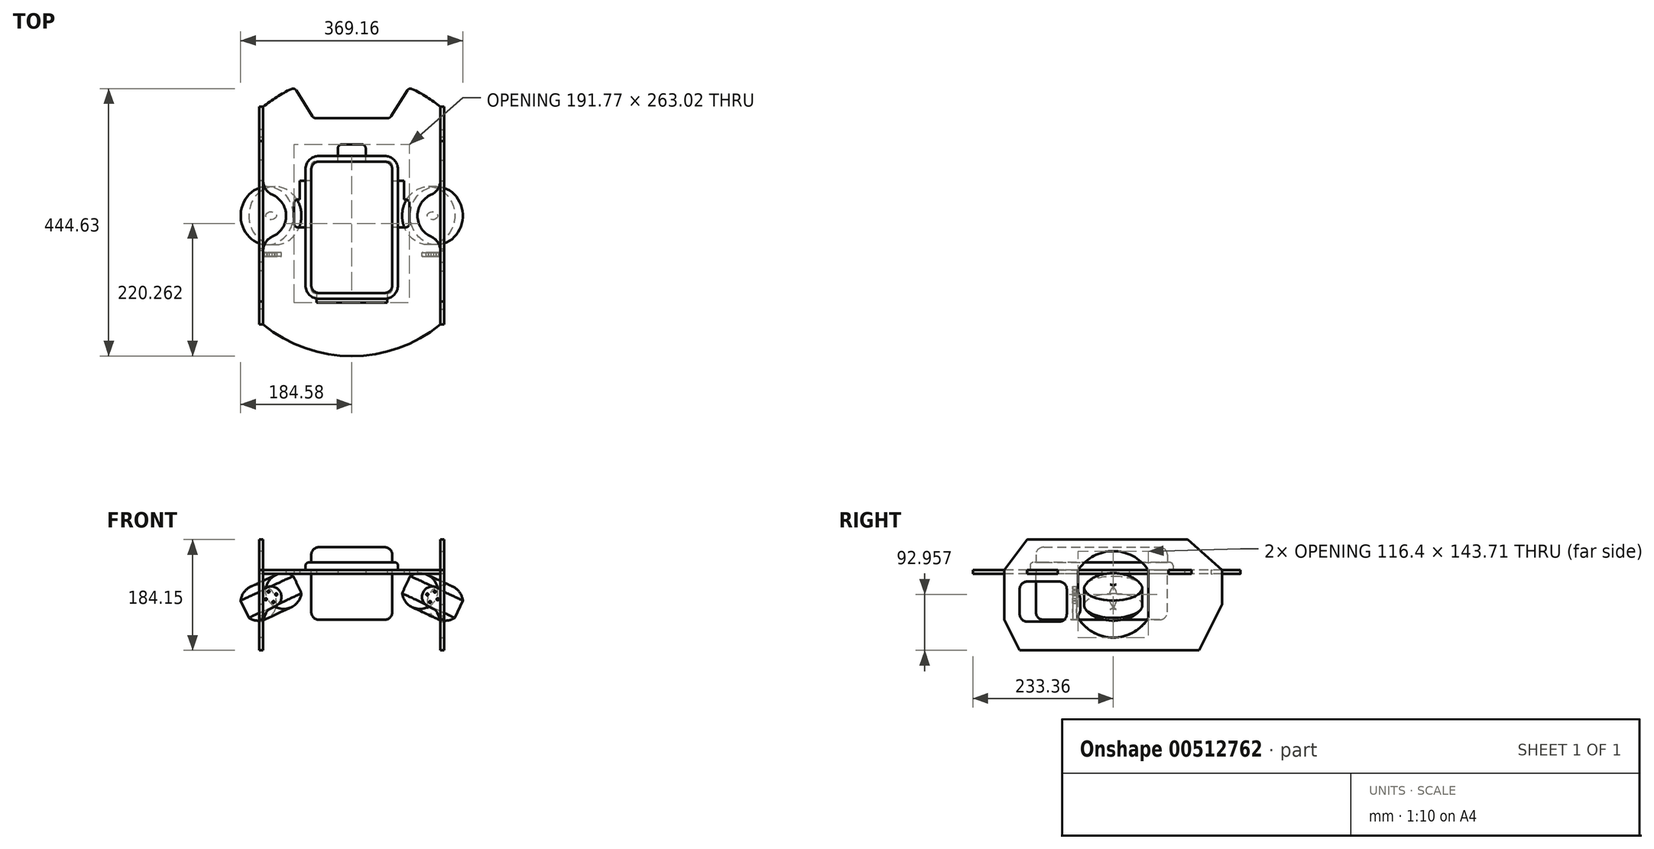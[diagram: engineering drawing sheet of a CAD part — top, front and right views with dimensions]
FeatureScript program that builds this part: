
annotation { "Feature Type Name" : "Feature", "Feature Type Description" : "" }
export const myFeature = defineFeature(function(context is Context, id is Id, definition is map)
    precondition{}
    {
        {
            var Q0;
            Q0=qCreatedBy(makeId("Top.planeOp"),FACE);
            var sketch = newSketch(context, id + "F0", { "sketchPlane" : qUnion([Q0])});
            skCircle(sketch, "E0", {"center": v(0, 0) * mm, "radius": 240 * mm, "construction": true});
            skSolve(sketch);
        }
        {
            var Q0;
            Q0=qCreatedBy(makeId("Top.planeOp"),FACE);
            var sketch = newSketch(context, id + "F1", { "sketchPlane" : qUnion([Q0])});
            skLineSegment(sketch, "E1", {"start": v(0, 0) * mm, "end": v(0, 264.4) * mm, "construction": true});
            skLineSegment(sketch, "E2", {"start": v(-67.31, 83.49) * mm, "end": v(-67.31, 58.09) * mm});
            skLineSegment(sketch, "E3", {"start": v(-67.3, 58.09) * mm, "end": v(-86.61, 58.09) * mm});
            skLineSegment(sketch, "E4", {"start": v(-86.61, 58.09) * mm, "end": v(-86.61, 26.84) * mm});
            skLineSegment(sketch, "E5", {"start": v(-86.61, 26.84) * mm, "end": v(-89.54, 26.84) * mm});
            skLineSegment(sketch, "E6", {"start": v(-95.89, 20.5) * mm, "end": v(-95.89, -13.03) * mm});
            skLineSegment(sketch, "E7", {"start": v(-89.54, -19.38) * mm, "end": v(-67.3, -19.38) * mm});
            skLineSegment(sketch, "E8", {"start": v(-67.31, -19.38) * mm, "end": v(-67.3, -122.25) * mm});
            skLineSegment(sketch, "E9", {"start": v(-60.96, -128.6) * mm, "end": v(-58.67, -128.6) * mm});
            skLineSegment(sketch, "E10", {"start": v(-60.96, 89.84) * mm, "end": v(-23.11, 89.84) * mm});
            skLineSegment(sketch, "E11", {"start": v(-23.11, 89.84) * mm, "end": v(-23.11, 112.06) * mm});
            skLineSegment(sketch, "E12.MirrorCS", {"start": v(86.61, 26.84) * mm, "end": v(89.54, 26.84) * mm});
            skLineSegment(sketch, "E13.MirrorCS", {"start": v(60.96, -128.6) * mm, "end": v(58.67, -128.6) * mm});
            skLineSegment(sketch, "E14.MirrorCS", {"start": v(67.31, 83.49) * mm, "end": v(67.31, 58.09) * mm});
            skLineSegment(sketch, "E15.MirrorCS", {"start": v(23.11, 89.84) * mm, "end": v(23.11, 112.06) * mm});
            skLineSegment(sketch, "E16.MirrorCS", {"start": v(67.3, 58.09) * mm, "end": v(86.61, 58.09) * mm});
            skLineSegment(sketch, "E17.MirrorCS", {"start": v(67.31, -19.38) * mm, "end": v(67.31, -122.25) * mm});
            skLineSegment(sketch, "E18.MirrorCS", {"start": v(89.54, -19.38) * mm, "end": v(67.3, -19.38) * mm});
            skLineSegment(sketch, "E19.MirrorCS", {"start": v(86.61, 58.09) * mm, "end": v(86.61, 26.84) * mm});
            skLineSegment(sketch, "E20.MirrorCS", {"start": v(95.89, 20.5) * mm, "end": v(95.89, -13.03) * mm});
            skLineSegment(sketch, "E21.MirrorCS", {"start": v(60.96, 89.84) * mm, "end": v(23.11, 89.84) * mm});
            skLineSegment(sketch, "E22", {"start": v(-58.67, -128.6) * mm, "end": v(-58.67, -144.6) * mm});
            skLineSegment(sketch, "E23.MirrorCS", {"start": v(58.67, -128.6) * mm, "end": v(58.67, -144.6) * mm});
            skLineSegment(sketch, "E24", {"start": v(-58.67, -144.6) * mm, "end": v(58.67, -144.6) * mm});
            skLineSegment(sketch, "E25", {"start": v(-16.76, 118.41) * mm, "end": v(16.76, 118.41) * mm});
            skPoint(sketch, "E26.visualSharp", {"position": v(-67.31, 89.84) * mm});
            skArc(sketch, "E26.filletArc", {"start": v(-60.96, 89.84) * mm, "mid": v(-65.45, 87.98) * mm, "end": v(-67.31, 83.49) * mm});
            skPoint(sketch, "E27.visualSharp", {"position": v(67.31, 89.84) * mm});
            skArc(sketch, "E27.filletArc", {"start": v(67.31, 83.49) * mm, "mid": v(65.45, 87.98) * mm, "end": v(60.96, 89.84) * mm});
            skPoint(sketch, "E28.visualSharp", {"position": v(23.11, 118.41) * mm});
            skArc(sketch, "E28.filletArc", {"start": v(23.11, 112.06) * mm, "mid": v(21.25, 116.55) * mm, "end": v(16.76, 118.41) * mm});
            skPoint(sketch, "E29.visualSharp", {"position": v(-23.11, 118.41) * mm});
            skArc(sketch, "E29.filletArc", {"start": v(-16.76, 118.41) * mm, "mid": v(-21.25, 116.55) * mm, "end": v(-23.11, 112.06) * mm});
            skPoint(sketch, "E30.visualSharp", {"position": v(-67.3, -128.6) * mm});
            skArc(sketch, "E30.filletArc", {"start": v(-67.3, -122.25) * mm, "mid": v(-65.45, -126.74) * mm, "end": v(-60.96, -128.6) * mm});
            skPoint(sketch, "E31.visualSharp", {"position": v(67.3, -128.6) * mm});
            skArc(sketch, "E31.filletArc", {"start": v(60.96, -128.6) * mm, "mid": v(65.45, -126.74) * mm, "end": v(67.31, -122.25) * mm});
            skPoint(sketch, "E32.visualSharp", {"position": v(95.89, -19.38) * mm});
            skArc(sketch, "E32.filletArc", {"start": v(89.54, -19.38) * mm, "mid": v(94.03, -17.52) * mm, "end": v(95.89, -13.03) * mm});
            skPoint(sketch, "E33.visualSharp", {"position": v(95.89, 26.84) * mm});
            skArc(sketch, "E33.filletArc", {"start": v(95.89, 20.5) * mm, "mid": v(94.03, 24.98) * mm, "end": v(89.54, 26.84) * mm});
            skPoint(sketch, "E34.visualSharp", {"position": v(-95.89, 26.84) * mm});
            skArc(sketch, "E34.filletArc", {"start": v(-89.54, 26.84) * mm, "mid": v(-94.03, 24.98) * mm, "end": v(-95.89, 20.5) * mm});
            skPoint(sketch, "E35.visualSharp", {"position": v(-95.89, -19.38) * mm});
            skArc(sketch, "E35.filletArc", {"start": v(-95.89, -13.03) * mm, "mid": v(-94.03, -17.52) * mm, "end": v(-89.54, -19.38) * mm});
            skLineSegment(sketch, "E36", {"start": v(-147.32, 180.98) * mm, "end": v(-147.32, 130.17) * mm});
            skLineSegment(sketch, "E37.MirrorCS", {"start": v(147.32, 180.98) * mm, "end": v(147.32, 130.17) * mm});
            skArc(sketch, "E38", {"start": v(147.32, 180.97) * mm, "mid": v(124.75, 197.21) * mm, "end": v(100.4, 210.65) * mm});
            skArc(sketch, "E39.trimOffspring", {"start": v(-147.32, -180.97) * mm, "mid": v(0, -233.36) * mm, "end": v(147.32, -180.97) * mm});
            skLineSegment(sketch, "E40", {"start": v(-92.28, 208.29) * mm, "end": v(-65.37, 165.22) * mm});
            skLineSegment(sketch, "E41", {"start": v(-59.98, 162.23) * mm, "end": v(0, 162.23) * mm});
            skLineSegment(sketch, "E42.MirrorCS", {"start": v(59.98, 162.23) * mm, "end": v(0, 162.23) * mm});
            skLineSegment(sketch, "E43.MirrorCS", {"start": v(92.28, 208.29) * mm, "end": v(65.37, 165.22) * mm});
            skArc(sketch, "E44.trimOffspring", {"start": v(-100.4, 210.65) * mm, "mid": v(-124.75, 197.21) * mm, "end": v(-147.32, 180.97) * mm});
            skPoint(sketch, "E45.visualSharp", {"position": v(-95.25, 213.03) * mm});
            skArc(sketch, "E45.filletArc", {"start": v(-92.28, 208.29) * mm, "mid": v(-95.9, 211.02) * mm, "end": v(-100.4, 210.65) * mm});
            skPoint(sketch, "E46.visualSharp", {"position": v(95.25, 213.03) * mm});
            skArc(sketch, "E46.filletArc", {"start": v(100.4, 210.65) * mm, "mid": v(95.9, 211.02) * mm, "end": v(92.28, 208.29) * mm});
            skPoint(sketch, "E47.visualSharp", {"position": v(-63.5, 162.23) * mm});
            skArc(sketch, "E47.filletArc", {"start": v(-65.37, 165.22) * mm, "mid": v(-63.06, 163.03) * mm, "end": v(-59.98, 162.23) * mm});
            skPoint(sketch, "E48.visualSharp", {"position": v(63.5, 162.23) * mm});
            skArc(sketch, "E48.filletArc", {"start": v(59.98, 162.23) * mm, "mid": v(63.06, 163.03) * mm, "end": v(65.37, 165.22) * mm});
            skArc(sketch, "E49", {"start": v(132.08, 34.92) * mm, "mid": v(109.22, 0) * mm, "end": v(132.08, -34.92) * mm});
            skArc(sketch, "E50.MirrorC", {"start": v(-132.08, 34.92) * mm, "mid": v(-109.22, 0) * mm, "end": v(-132.08, -34.92) * mm});
            skLineSegment(sketch, "E51.trimOffspring", {"start": v(147.32, -58.2) * mm, "end": v(147.32, -92.07) * mm});
            skLineSegment(sketch, "E52.trimOffspring", {"start": v(-147.32, -58.2) * mm, "end": v(-147.32, -92.07) * mm});
            skPoint(sketch, "E53.visualSharp", {"position": v(147.32, 38.1) * mm});
            skArc(sketch, "E53.filletArc", {"start": v(132.08, 34.92) * mm, "mid": v(143.17, 44.29) * mm, "end": v(147.32, 58.2) * mm});
            skPoint(sketch, "E54.visualSharp", {"position": v(147.32, -38.1) * mm});
            skArc(sketch, "E54.filletArc", {"start": v(147.32, -58.2) * mm, "mid": v(143.17, -44.29) * mm, "end": v(132.08, -34.92) * mm});
            skPoint(sketch, "E55.visualSharp", {"position": v(-147.32, -38.1) * mm});
            skArc(sketch, "E55.filletArc", {"start": v(-132.08, -34.92) * mm, "mid": v(-143.17, -44.29) * mm, "end": v(-147.32, -58.2) * mm});
            skPoint(sketch, "E56.visualSharp", {"position": v(-147.32, 38.1) * mm});
            skArc(sketch, "E56.filletArc", {"start": v(-147.32, 58.2) * mm, "mid": v(-143.17, 44.29) * mm, "end": v(-132.08, 34.92) * mm});
            skLineSegment(sketch, "E57", {"start": v(147.32, 92.07) * mm, "end": v(153.67, 92.07) * mm});
            skLineSegment(sketch, "E58", {"start": v(153.67, 92.07) * mm, "end": v(153.67, 130.17) * mm});
            skLineSegment(sketch, "E59", {"start": v(153.67, 130.17) * mm, "end": v(147.32, 130.17) * mm});
            skLineSegment(sketch, "E60.MirrorCS", {"start": v(-153.67, 92.07) * mm, "end": v(-153.67, 130.17) * mm});
            skLineSegment(sketch, "E61.MirrorCS", {"start": v(-147.32, 92.07) * mm, "end": v(-153.67, 92.07) * mm});
            skLineSegment(sketch, "E62.MirrorCS", {"start": v(-153.67, 130.17) * mm, "end": v(-147.32, 130.17) * mm});
            skLineSegment(sketch, "E63.trimOffspring", {"start": v(-147.32, 92.07) * mm, "end": v(-147.32, 58.2) * mm});
            skLineSegment(sketch, "E64.trimOffspring", {"start": v(147.32, 92.07) * mm, "end": v(147.32, 58.2) * mm});
            skLineSegment(sketch, "E65", {"start": v(147.32, -92.07) * mm, "end": v(153.67, -92.07) * mm});
            skLineSegment(sketch, "E66", {"start": v(153.67, -92.07) * mm, "end": v(153.67, -142.87) * mm});
            skLineSegment(sketch, "E67", {"start": v(153.67, -142.87) * mm, "end": v(147.32, -142.87) * mm});
            skLineSegment(sketch, "E68.MirrorCS", {"start": v(-153.67, -92.07) * mm, "end": v(-153.67, -142.87) * mm});
            skLineSegment(sketch, "E69.MirrorCS", {"start": v(-147.32, -92.07) * mm, "end": v(-153.67, -92.07) * mm});
            skLineSegment(sketch, "E70.MirrorCS", {"start": v(-153.67, -142.87) * mm, "end": v(-147.32, -142.87) * mm});
            skLineSegment(sketch, "E71.trimOffspring", {"start": v(147.32, -142.87) * mm, "end": v(147.32, -180.97) * mm});
            skLineSegment(sketch, "E72.trimOffspring", {"start": v(-147.32, -142.87) * mm, "end": v(-147.32, -180.97) * mm});
            skSolve(sketch);
        }
        {
            var Q0;
            Q0=makeQuery(id+"F1.imprint","IMPRINT",FACE,{"disambiguationData":[TD([[makeQuery(id+"F1.imprint","IMPRINT",EDGE,{"derivedFrom":sQuery(id+"F1.wireOp",EDGE,"E2")}),-1.0]])]});
            extrude(context, id + "F2", {"entities" : qUnion([Q0]), "depth" : 6.35 * mm, "offsetDistance" : 25.4 * mm});
        }
        {
            var Q0;
            Q0=makeQuery(id+"F2.opExtrude","CAP_FACE",FACE,{"disambiguationData":[OSD([sQuery(id+"F1.wireOp",EDGE,"E2"),sQuery(id+"F1.wireOp",EDGE,"E3"),sQuery(id+"F1.wireOp",EDGE,"E4"),sQuery(id+"F1.wireOp",EDGE,"E5"),sQuery(id+"F1.wireOp",EDGE,"E6"),sQuery(id+"F1.wireOp",EDGE,"E7"),sQuery(id+"F1.wireOp",EDGE,"E8"),sQuery(id+"F1.wireOp",EDGE,"E9"),sQuery(id+"F1.wireOp",EDGE,"E10"),sQuery(id+"F1.wireOp",EDGE,"E11"),sQuery(id+"F1.wireOp",EDGE,"E12.MirrorCS"),sQuery(id+"F1.wireOp",EDGE,"E13.MirrorCS"),sQuery(id+"F1.wireOp",EDGE,"E14.MirrorCS"),sQuery(id+"F1.wireOp",EDGE,"E15.MirrorCS"),sQuery(id+"F1.wireOp",EDGE,"E16.MirrorCS"),sQuery(id+"F1.wireOp",EDGE,"E17.MirrorCS"),sQuery(id+"F1.wireOp",EDGE,"E18.MirrorCS"),sQuery(id+"F1.wireOp",EDGE,"E19.MirrorCS"),sQuery(id+"F1.wireOp",EDGE,"E20.MirrorCS"),sQuery(id+"F1.wireOp",EDGE,"E21.MirrorCS"),sQuery(id+"F1.wireOp",EDGE,"E22"),sQuery(id+"F1.wireOp",EDGE,"E23.MirrorCS"),sQuery(id+"F1.wireOp",EDGE,"E24"),sQuery(id+"F1.wireOp",EDGE,"E25"),sQuery(id+"F1.wireOp",EDGE,"E26.filletArc"),sQuery(id+"F1.wireOp",EDGE,"E27.filletArc"),sQuery(id+"F1.wireOp",EDGE,"E28.filletArc"),sQuery(id+"F1.wireOp",EDGE,"E29.filletArc"),sQuery(id+"F1.wireOp",EDGE,"E30.filletArc"),sQuery(id+"F1.wireOp",EDGE,"E31.filletArc"),sQuery(id+"F1.wireOp",EDGE,"E32.filletArc"),sQuery(id+"F1.wireOp",EDGE,"E33.filletArc"),sQuery(id+"F1.wireOp",EDGE,"E34.filletArc"),sQuery(id+"F1.wireOp",EDGE,"E35.filletArc"),sQuery(id+"F1.wireOp",EDGE,"E37.MirrorCS"),sQuery(id+"F1.wireOp",EDGE,"E38"),sQuery(id+"F1.wireOp",EDGE,"E39.trimOffspring"),sQuery(id+"F1.wireOp",EDGE,"E40"),sQuery(id+"F1.wireOp",EDGE,"E41"),sQuery(id+"F1.wireOp",EDGE,"E42.MirrorCS"),sQuery(id+"F1.wireOp",EDGE,"E43.MirrorCS"),sQuery(id+"F1.wireOp",EDGE,"E44.trimOffspring"),sQuery(id+"F1.wireOp",EDGE,"E45.filletArc"),sQuery(id+"F1.wireOp",EDGE,"E46.filletArc"),sQuery(id+"F1.wireOp",EDGE,"E47.filletArc"),sQuery(id+"F1.wireOp",EDGE,"E48.filletArc"),sQuery(id+"F1.wireOp",EDGE,"E49"),sQuery(id+"F1.wireOp",EDGE,"E50.MirrorC"),sQuery(id+"F1.wireOp",EDGE,"E51.trimOffspring"),sQuery(id+"F1.wireOp",EDGE,"E52.trimOffspring"),sQuery(id+"F1.wireOp",EDGE,"E53.filletArc"),sQuery(id+"F1.wireOp",EDGE,"E54.filletArc"),sQuery(id+"F1.wireOp",EDGE,"E55.filletArc"),sQuery(id+"F1.wireOp",EDGE,"E56.filletArc"),sQuery(id+"F1.wireOp",EDGE,"E57"),sQuery(id+"F1.wireOp",EDGE,"E58"),sQuery(id+"F1.wireOp",EDGE,"E59"),sQuery(id+"F1.wireOp",EDGE,"E60.MirrorCS"),sQuery(id+"F1.wireOp",EDGE,"E36"),sQuery(id+"F1.wireOp",EDGE,"E61.MirrorCS"),sQuery(id+"F1.wireOp",EDGE,"E62.MirrorCS"),sQuery(id+"F1.wireOp",EDGE,"E64.trimOffspring"),sQuery(id+"F1.wireOp",EDGE,"E63.trimOffspring"),sQuery(id+"F1.wireOp",EDGE,"E65"),sQuery(id+"F1.wireOp",EDGE,"E66"),sQuery(id+"F1.wireOp",EDGE,"E67"),sQuery(id+"F1.wireOp",EDGE,"E68.MirrorCS"),sQuery(id+"F1.wireOp",EDGE,"E69.MirrorCS"),sQuery(id+"F1.wireOp",EDGE,"E70.MirrorCS"),sQuery(id+"F1.wireOp",EDGE,"E71.trimOffspring"),sQuery(id+"F1.wireOp",EDGE,"E72.trimOffspring")])],"isStart":false});
            var sketch = newSketch(context, id + "F3", { "sketchPlane" : qUnion([Q0])});
            skPoint(sketch, "E73.0", {"position": v(-67.3, -128.6) * mm});
            skPoint(sketch, "E74.0", {"position": v(-67.31, 89.84) * mm});
            skPoint(sketch, "E75.0", {"position": v(67.31, 89.84) * mm});
            skPoint(sketch, "E76.0", {"position": v(67.3, -128.6) * mm});
            skLineSegment(sketch, "E77", {"start": v(-67.3, -115.9) * mm, "end": v(-67.31, 77.14) * mm});
            skLineSegment(sketch, "E78", {"start": v(54.61, 89.84) * mm, "end": v(-54.61, 89.84) * mm});
            skLineSegment(sketch, "E79", {"start": v(-54.6, -128.6) * mm, "end": v(54.6, -128.6) * mm});
            skLineSegment(sketch, "E80", {"start": v(67.3, -115.9) * mm, "end": v(67.31, 77.14) * mm});
            skArc(sketch, "E81.filletArc", {"start": v(-67.3, -115.9) * mm, "mid": v(-63.6, -124.88) * mm, "end": v(-54.6, -128.6) * mm});
            skArc(sketch, "E82.filletArc", {"start": v(54.6, -128.6) * mm, "mid": v(63.6, -124.88) * mm, "end": v(67.3, -115.9) * mm});
            skArc(sketch, "E83.filletArc", {"start": v(67.31, 77.14) * mm, "mid": v(63.6, 86.12) * mm, "end": v(54.61, 89.84) * mm});
            skArc(sketch, "E84.filletArc", {"start": v(-54.61, 89.84) * mm, "mid": v(-63.6, 86.12) * mm, "end": v(-67.31, 77.14) * mm});
            skSolve(sketch);
        }
        {
            var Q0;
            Q0=makeQuery(id+"F3.imprint","IMPRINT",FACE,{"disambiguationData":[TD([[makeQuery(id+"F3.imprint","IMPRINT",EDGE,{"derivedFrom":sQuery(id+"F3.wireOp",EDGE,"E79")}),1.0]])]});
            extrude(context, id + "F4", {"entities" : qUnion([Q0]), "oppositeDirection" : true, "depth" : 82.55 * mm, "offsetDistance" : 25.4 * mm});
        }
        {
            var Q0;
            Q0=makeQuery(id+"F4.opExtrude","CAP_EDGE",EDGE,{"disambiguationData":[OSD([sQuery(id+"F3.wireOp",EDGE,"E77")])],"isStart":false});
            fillet(context, id + "F5", {"entities" : qUnion([Q0]), "radius" : 12.7 * mm, "tangentPropagation" : true, "allowEdgeOverflow" : false});
        }
        {
            var Q0;
            Q0=qCreatedBy(makeId("Front.planeOp"),FACE);
            var sketch = newSketch(context, id + "F6", { "sketchPlane" : qUnion([Q0])});
            skLineSegment(sketch, "E85", {"start": v(121.44, -65.48) * mm, "end": v(146.05, -12.7) * mm, "construction": true});
            skLineSegment(sketch, "E86", {"start": v(184.58, -44.26) * mm, "end": v(171.16, -73.04) * mm});
            skArc(sketch, "E87", {"start": v(171.16, -73.04) * mm, "mid": v(182.03, -60.59) * mm, "end": v(184.58, -44.26) * mm});
            skLineSegment(sketch, "E88", {"start": v(146.05, -12.7) * mm, "end": v(146.05, -91.7) * mm, "construction": true});
            skSolve(sketch);
        }
        {
            var Q0;
            Q0=makeQuery(id+"F6.imprint","IMPRINT",FACE,{"disambiguationData":[TD([[makeQuery(id+"F6.imprint","IMPRINT",EDGE,{"derivedFrom":sQuery(id+"F6.wireOp",EDGE,"E86")}),1.0]])]});
            var Q1;
            Q1=sQuery(id+"F6.wireOp",EDGE,"E85");
            revolve(context, id + "F7", {"entities" : qUnion([Q0]), "axis" : qUnion([Q1]), "revolveType" : RevolveType.FULL});
        }
        {
            var Q0;
            Q0=makeQuery(id+"F7.opRevolve","SWEPT_BODY",BODY,{"disambiguationData":[OSD([sQuery(id+"F6.wireOp",EDGE,"E86"),sQuery(id+"F6.wireOp",EDGE,"E87")])]});
            var Q1;
            Q1=qCreatedBy(makeId("Right.planeOp"),FACE);
            mirror(context, id + "F8", {"entities" : qUnion([Q0]), "mirrorPlane" : qUnion([Q1])});
        }
        {
            var Q0;
            Q0=makeQuery(id+"F2.opExtrude","SWEPT_FACE",FACE,{"disambiguationData":[OSD([sQuery(id+"F1.wireOp",EDGE,"E66")])]});
            var sketch = newSketch(context, id + "F9", { "sketchPlane" : qUnion([Q0])});
            skLineSegment(sketch, "E89.0.0", {"start": v(-142.87, 0) * mm, "end": v(-92.07, 0) * mm});
            skLineSegment(sketch, "E89.0.1", {"start": v(-92.07, 0) * mm, "end": v(-92.07, 6.35) * mm});
            skLineSegment(sketch, "E89.0.2", {"start": v(-92.07, 6.35) * mm, "end": v(-142.87, 6.35) * mm});
            skLineSegment(sketch, "E89.0.3", {"start": v(-142.87, 6.35) * mm, "end": v(-142.87, 0) * mm});
            skLineSegment(sketch, "E90.0.0", {"start": v(92.07, 0) * mm, "end": v(130.17, 0) * mm});
            skLineSegment(sketch, "E90.0.1", {"start": v(130.17, 0) * mm, "end": v(130.17, 6.35) * mm});
            skLineSegment(sketch, "E90.0.2", {"start": v(130.17, 6.35) * mm, "end": v(92.07, 6.35) * mm});
            skLineSegment(sketch, "E90.0.3", {"start": v(92.07, 6.35) * mm, "end": v(92.07, 0) * mm});
            skPoint(sketch, "E91.0", {"position": v(180.97, 6.35) * mm});
            skPoint(sketch, "E92.0", {"position": v(-180.98, 6.35) * mm});
            skLineSegment(sketch, "E93", {"start": v(-180.98, 6.35) * mm, "end": v(-142.88, 57.15) * mm});
            skLineSegment(sketch, "E94", {"start": v(-142.88, 57.15) * mm, "end": v(123.82, 57.15) * mm});
            skLineSegment(sketch, "E95", {"start": v(123.82, 57.15) * mm, "end": v(180.98, 6.35) * mm});
            skLineSegment(sketch, "E96", {"start": v(180.97, 6.35) * mm, "end": v(180.97, -50.8) * mm});
            skLineSegment(sketch, "E97", {"start": v(180.98, -50.8) * mm, "end": v(142.88, -127) * mm});
            skLineSegment(sketch, "E98", {"start": v(142.88, -127) * mm, "end": v(-155.58, -127) * mm});
            skLineSegment(sketch, "E99", {"start": v(-155.57, -127) * mm, "end": v(-180.98, -76.2) * mm});
            skLineSegment(sketch, "E100", {"start": v(-180.98, -76.2) * mm, "end": v(-180.98, 6.35) * mm});
            skPoint(sketch, "E101.0", {"position": v(-58.2, 6.35) * mm});
            skPoint(sketch, "E102.0", {"position": v(58.2, 6.35) * mm});
            skArc(sketch, "E103", {"start": v(57.06, 8.04) * mm, "mid": v(0, 37.81) * mm, "end": v(-57.06, 8.04) * mm});
            skLineSegment(sketch, "E104", {"start": v(-58.2, 4.4) * mm, "end": v(-58.2, 0) * mm});
            skLineSegment(sketch, "E105", {"start": v(-58.2, 0) * mm, "end": v(-58.2, -30.25) * mm});
            skLineSegment(sketch, "E106", {"start": v(-57.53, -33.1) * mm, "end": v(-55.7, -36.76) * mm});
            skLineSegment(sketch, "E107", {"start": v(-55.02, -39.6) * mm, "end": v(-55.02, -62) * mm});
            skLineSegment(sketch, "E108", {"start": v(-55.7, -64.84) * mm, "end": v(-58.2, -69.85) * mm});
            skLineSegment(sketch, "E109", {"start": v(-58.2, -69.85) * mm, "end": v(-58.2, -73.02) * mm});
            skLineSegment(sketch, "E110", {"start": v(58.2, -73.02) * mm, "end": v(58.2, 4.4) * mm});
            skPoint(sketch, "E111.visualSharp", {"position": v(-58.2, -79.38) * mm});
            skPoint(sketch, "E112.visualSharp", {"position": v(58.2, -79.37) * mm});
            skArc(sketch, "E113.filletArc", {"start": v(58.2, 4.4) * mm, "mid": v(57.9, 6.31) * mm, "end": v(57.06, 8.04) * mm});
            skArc(sketch, "E114.filletArc", {"start": v(-57.06, 8.04) * mm, "mid": v(-57.9, 6.31) * mm, "end": v(-58.2, 4.4) * mm});
            skPoint(sketch, "E115.visualSharp", {"position": v(-58.2, -31.75) * mm});
            skArc(sketch, "E115.filletArc", {"start": v(-58.2, -30.25) * mm, "mid": v(-58.03, -31.7) * mm, "end": v(-57.53, -33.1) * mm});
            skPoint(sketch, "E116.visualSharp", {"position": v(-55.02, -38.1) * mm});
            skArc(sketch, "E116.filletArc", {"start": v(-55.02, -39.6) * mm, "mid": v(-55.2, -38.14) * mm, "end": v(-55.7, -36.76) * mm});
            skPoint(sketch, "E117.visualSharp", {"position": v(-55.02, -63.5) * mm});
            skArc(sketch, "E117.filletArc", {"start": v(-55.7, -64.84) * mm, "mid": v(-55.2, -63.46) * mm, "end": v(-55.02, -62) * mm});
            skArc(sketch, "E118", {"start": v(-58.2, -73.02) * mm, "mid": v(0, -105.9) * mm, "end": v(58.2, -73.03) * mm});
            skSolve(sketch);
        }
        {
            var Q0;
            Q0=makeQuery(id+"F9.imprint","IMPRINT",FACE,{"disambiguationData":[TD([[makeQuery(id+"F9.imprint","IMPRINT",EDGE,{"derivedFrom":sQuery(id+"F9.wireOp",EDGE,"E89.0.0")}),1.0]])]});
            var sketch = newSketch(context, id + "F10", { "sketchPlane" : qUnion([Q0])});
            skLineSegment(sketch, "E119", {"start": v(-89.95, -12.7) * mm, "end": v(-142.88, -12.7) * mm});
            skLineSegment(sketch, "E120", {"start": v(-155.58, -25.4) * mm, "end": v(-155.58, -66.67) * mm});
            skLineSegment(sketch, "E121", {"start": v(-142.88, -79.37) * mm, "end": v(-89.95, -79.37) * mm});
            skLineSegment(sketch, "E122", {"start": v(-77.25, -66.67) * mm, "end": v(-77.25, -25.4) * mm});
            skPoint(sketch, "E123.visualSharp", {"position": v(-155.58, -12.7) * mm});
            skArc(sketch, "E123.filletArc", {"start": v(-142.88, -12.7) * mm, "mid": v(-151.86, -16.42) * mm, "end": v(-155.58, -25.4) * mm});
            skPoint(sketch, "E124.visualSharp", {"position": v(-77.25, -12.7) * mm});
            skArc(sketch, "E124.filletArc", {"start": v(-77.25, -25.4) * mm, "mid": v(-80.97, -16.42) * mm, "end": v(-89.95, -12.7) * mm});
            skPoint(sketch, "E125.visualSharp", {"position": v(-77.25, -79.37) * mm});
            skArc(sketch, "E125.filletArc", {"start": v(-89.95, -79.37) * mm, "mid": v(-80.97, -75.66) * mm, "end": v(-77.25, -66.67) * mm});
            skPoint(sketch, "E126.visualSharp", {"position": v(-155.58, -79.37) * mm});
            skArc(sketch, "E126.filletArc", {"start": v(-155.58, -66.67) * mm, "mid": v(-151.86, -75.66) * mm, "end": v(-142.88, -79.38) * mm});
            skSolve(sketch);
        }
        {
            var Q0;
            Q0=makeQuery(id+"F9.imprint","IMPRINT",FACE,{"disambiguationData":[TD([[makeQuery(id+"F9.imprint","IMPRINT",EDGE,{"derivedFrom":sQuery(id+"F9.wireOp",EDGE,"E89.0.0")}),1.0]])]});
            extrude(context, id + "F11", {"entities" : qUnion([Q0]), "oppositeDirection" : true, "depth" : 6.35 * mm, "offsetDistance" : 25.4 * mm});
        }
        {
            var Q0;
            Q0=makeQuery(id+"F10.imprint","IMPRINT",FACE,{"disambiguationData":[TD([[makeQuery(id+"F10.imprint","IMPRINT",EDGE,{"derivedFrom":sQuery(id+"F10.wireOp",EDGE,"E119")}),1.0]])]});
            extrude(context, id + "F12", {"entities" : qUnion([Q0]), "operationType" : NewBodyOperationType.REMOVE, "oppositeDirection" : true, "depth" : 25.4 * mm, "offsetDistance" : 25.4 * mm});
        }
        {
            var Q0;
            Q0=makeQuery(id+"F11.opExtrude","CAP_FACE",FACE,{"disambiguationData":[OSD([sQuery(id+"F9.wireOp",EDGE,"E89.0.0"),sQuery(id+"F9.wireOp",EDGE,"E89.0.1"),sQuery(id+"F9.wireOp",EDGE,"E89.0.2"),sQuery(id+"F9.wireOp",EDGE,"E89.0.3"),sQuery(id+"F9.wireOp",EDGE,"E90.0.0"),sQuery(id+"F9.wireOp",EDGE,"E90.0.1"),sQuery(id+"F9.wireOp",EDGE,"E90.0.2"),sQuery(id+"F9.wireOp",EDGE,"E90.0.3"),sQuery(id+"F9.wireOp",EDGE,"E93"),sQuery(id+"F9.wireOp",EDGE,"E94"),sQuery(id+"F9.wireOp",EDGE,"E95"),sQuery(id+"F9.wireOp",EDGE,"E96"),sQuery(id+"F9.wireOp",EDGE,"E97"),sQuery(id+"F9.wireOp",EDGE,"E98"),sQuery(id+"F9.wireOp",EDGE,"E99"),sQuery(id+"F9.wireOp",EDGE,"E100"),sQuery(id+"F9.wireOp",EDGE,"E103"),sQuery(id+"F9.wireOp",EDGE,"E104"),sQuery(id+"F9.wireOp",EDGE,"E105"),sQuery(id+"F9.wireOp",EDGE,"E106"),sQuery(id+"F9.wireOp",EDGE,"E107"),sQuery(id+"F9.wireOp",EDGE,"E108"),sQuery(id+"F9.wireOp",EDGE,"E109"),sQuery(id+"F9.wireOp",EDGE,"OLEld7MS-5iyU-KDxF-mcr4-tdyzlXDpxbxK"),sQuery(id+"F9.wireOp",EDGE,"E110"),sQuery(id+"F9.wireOp",EDGE,"E111.filletArc"),sQuery(id+"F9.wireOp",EDGE,"E112.filletArc"),sQuery(id+"F9.wireOp",EDGE,"E113.filletArc"),sQuery(id+"F9.wireOp",EDGE,"E114.filletArc"),sQuery(id+"F9.wireOp",EDGE,"E115.filletArc"),sQuery(id+"F9.wireOp",EDGE,"E116.filletArc"),sQuery(id+"F9.wireOp",EDGE,"E117.filletArc")])],"isStart":true});
            var sketch = newSketch(context, id + "F13", { "sketchPlane" : qUnion([Q0])});
            skLineSegment(sketch, "E127.bottom", {"start": v(-67.72, -38.1) * mm, "end": v(-61.37, -38.1) * mm});
            skLineSegment(sketch, "E127.top", {"start": v(-67.72, -63.5) * mm, "end": v(-61.37, -63.5) * mm});
            skLineSegment(sketch, "E127.left", {"start": v(-67.72, -38.1) * mm, "end": v(-67.72, -63.5) * mm});
            skLineSegment(sketch, "E127.right", {"start": v(-61.37, -38.1) * mm, "end": v(-61.37, -63.5) * mm});
            skSolve(sketch);
        }
        {
            var Q0;
            Q0=makeQuery(id+"F13.imprint","IMPRINT",FACE,{"disambiguationData":[TD([[makeQuery(id+"F13.imprint","IMPRINT",EDGE,{"derivedFrom":sQuery(id+"F13.wireOp",EDGE,"E127.bottom")}),-1.0]])]});
            extrude(context, id + "F14", {"entities" : qUnion([Q0]), "operationType" : NewBodyOperationType.REMOVE, "oppositeDirection" : true, "depth" : 25.4 * mm, "offsetDistance" : 25.4 * mm});
        }
        {
            var Q0;
            Q0=makeQuery(id+"F4.opExtrude","CAP_FACE",FACE,{"disambiguationData":[OSD([sQuery(id+"F3.wireOp",EDGE,"E77"),sQuery(id+"F3.wireOp",EDGE,"E78"),sQuery(id+"F3.wireOp",EDGE,"E79"),sQuery(id+"F3.wireOp",EDGE,"E80"),sQuery(id+"F3.wireOp",EDGE,"E81.filletArc"),sQuery(id+"F3.wireOp",EDGE,"E82.filletArc"),sQuery(id+"F3.wireOp",EDGE,"E83.filletArc"),sQuery(id+"F3.wireOp",EDGE,"E84.filletArc")])],"isStart":true});
            var sketch = newSketch(context, id + "F15", { "sketchPlane" : qUnion([Q0])});
            skLineSegment(sketch, "E128.0.0", {"start": v(54.61, 89.84) * mm, "end": v(-54.61, 89.84) * mm});
            skArc(sketch, "E128.0.1", {"start": v(-54.61, 89.84) * mm, "mid": v(-63.6, 86.12) * mm, "end": v(-67.31, 77.14) * mm});
            skLineSegment(sketch, "E128.0.2", {"start": v(-67.31, 77.14) * mm, "end": v(-67.3, -115.9) * mm});
            skArc(sketch, "E128.0.3", {"start": v(-67.3, -115.9) * mm, "mid": v(-63.6, -124.88) * mm, "end": v(-54.6, -128.6) * mm});
            skLineSegment(sketch, "E128.0.4", {"start": v(-54.6, -128.6) * mm, "end": v(54.6, -128.6) * mm});
            skArc(sketch, "E128.0.5", {"start": v(54.6, -128.6) * mm, "mid": v(63.6, -124.88) * mm, "end": v(67.3, -115.9) * mm});
            skLineSegment(sketch, "E128.0.6", {"start": v(67.31, -115.9) * mm, "end": v(67.31, 77.14) * mm});
            skArc(sketch, "E128.0.7", {"start": v(67.31, 77.14) * mm, "mid": v(63.6, 86.12) * mm, "end": v(54.61, 89.84) * mm});
            skArc(sketch, "E129.0", {"start": v(-54.61, 99.36) * mm, "mid": v(-70.33, 92.85) * mm, "end": v(-76.84, 77.14) * mm});
            skLineSegment(sketch, "E129.1", {"start": v(54.61, 99.36) * mm, "end": v(-54.61, 99.36) * mm});
            skLineSegment(sketch, "E129.2", {"start": v(-76.84, 77.14) * mm, "end": v(-76.83, -115.9) * mm});
            skArc(sketch, "E129.3", {"start": v(76.84, 77.14) * mm, "mid": v(70.33, 92.85) * mm, "end": v(54.61, 99.36) * mm});
            skArc(sketch, "E129.4", {"start": v(-76.83, -115.9) * mm, "mid": v(-70.33, -131.62) * mm, "end": v(-54.6, -138.13) * mm});
            skLineSegment(sketch, "E129.5", {"start": v(-54.6, -138.13) * mm, "end": v(54.6, -138.13) * mm});
            skArc(sketch, "E129.6", {"start": v(54.6, -138.13) * mm, "mid": v(70.33, -131.62) * mm, "end": v(76.83, -115.9) * mm});
            skLineSegment(sketch, "E129.7", {"start": v(76.84, -115.9) * mm, "end": v(76.84, 77.14) * mm});
            skSolve(sketch);
        }
        {
            var Q0;
            Q0=makeQuery(id+"F15.imprint","IMPRINT",FACE,{"disambiguationData":[TD([[makeQuery(id+"F15.imprint","IMPRINT",EDGE,{"derivedFrom":sQuery(id+"F15.wireOp",EDGE,"E128.0.0")}),1.0]])]});
            var Q1;
            Q1=makeQuery(id+"F15.imprint","IMPRINT",FACE,{"disambiguationData":[TD([[makeQuery(id+"F15.imprint","IMPRINT",EDGE,{"derivedFrom":sQuery(id+"F15.wireOp",EDGE,"E128.0.0")}),-1.0]])]});
            extrude(context, id + "F16", {"entities" : qUnion([Q0, Q1]), "depth" : 12.7 * mm, "offsetDistance" : 25.4 * mm});
        }
        {
            var Q0;
            Q0=makeQuery(id+"F16.opExtrude","CAP_FACE",FACE,{"disambiguationData":[OSD([sQuery(id+"F15.wireOp",EDGE,"E129.0"),sQuery(id+"F15.wireOp",EDGE,"E129.1"),sQuery(id+"F15.wireOp",EDGE,"E129.2"),sQuery(id+"F15.wireOp",EDGE,"E129.3"),sQuery(id+"F15.wireOp",EDGE,"E129.4"),sQuery(id+"F15.wireOp",EDGE,"E129.5"),sQuery(id+"F15.wireOp",EDGE,"E129.6"),sQuery(id+"F15.wireOp",EDGE,"E129.7")])],"isStart":false});
            var sketch = newSketch(context, id + "F17", { "sketchPlane" : qUnion([Q0])});
            skLineSegment(sketch, "E130.0.0", {"start": v(54.61, 89.84) * mm, "end": v(-54.61, 89.84) * mm});
            skArc(sketch, "E130.0.1", {"start": v(-54.61, 89.84) * mm, "mid": v(-63.6, 86.12) * mm, "end": v(-67.31, 77.14) * mm});
            skLineSegment(sketch, "E130.0.2", {"start": v(-67.31, 77.14) * mm, "end": v(-67.3, -115.9) * mm});
            skArc(sketch, "E130.0.3", {"start": v(-67.3, -115.9) * mm, "mid": v(-63.6, -124.88) * mm, "end": v(-54.6, -128.6) * mm});
            skLineSegment(sketch, "E130.0.4", {"start": v(-54.6, -128.6) * mm, "end": v(54.6, -128.6) * mm});
            skArc(sketch, "E130.0.5", {"start": v(54.6, -128.6) * mm, "mid": v(63.6, -124.88) * mm, "end": v(67.3, -115.9) * mm});
            skLineSegment(sketch, "E130.0.6", {"start": v(67.31, -115.9) * mm, "end": v(67.31, 77.14) * mm});
            skArc(sketch, "E130.0.7", {"start": v(67.31, 77.14) * mm, "mid": v(63.6, 86.12) * mm, "end": v(54.61, 89.84) * mm});
            skSolve(sketch);
        }
        {
            var Q0;
            Q0=makeQuery(id+"F17.imprint","IMPRINT",FACE,{"disambiguationData":[TD([[makeQuery(id+"F17.imprint","IMPRINT",EDGE,{"derivedFrom":sQuery(id+"F17.wireOp",EDGE,"E130.0.0")}),1.0]])]});
            extrude(context, id + "F18", {"entities" : qUnion([Q0]), "operationType" : NewBodyOperationType.ADD, "depth" : 25.4 * mm, "offsetDistance" : 25.4 * mm});
        }
        {
            var Q0;
            Q0=makeQuery(id+"F16.opExtrude","CAP_EDGE",EDGE,{"disambiguationData":[OSD([sQuery(id+"F15.wireOp",EDGE,"E129.2")])],"isStart":false});
            fillet(context, id + "F19", {"entities" : qUnion([Q0]), "radius" : 5.08 * mm, "tangentPropagation" : true, "allowEdgeOverflow" : false});
        }
        {
            var Q0;
            Q0=makeQuery(id+"F18.opExtrude","CAP_EDGE",EDGE,{"disambiguationData":[OSD([sQuery(id+"F17.wireOp",EDGE,"E130.0.2")])],"isStart":false});
            fillet(context, id + "F20", {"entities" : qUnion([Q0]), "radius" : 12.7 * mm, "tangentPropagation" : true, "allowEdgeOverflow" : false});
        }
        {
            var Q0;
            Q0=makeQuery(id+"F11.opExtrude","SWEPT_BODY",BODY,{"disambiguationData":[OSD([sQuery(id+"F9.wireOp",EDGE,"E89.0.0"),sQuery(id+"F9.wireOp",EDGE,"E89.0.1"),sQuery(id+"F9.wireOp",EDGE,"E89.0.2"),sQuery(id+"F9.wireOp",EDGE,"E89.0.3"),sQuery(id+"F9.wireOp",EDGE,"E90.0.0"),sQuery(id+"F9.wireOp",EDGE,"E90.0.1"),sQuery(id+"F9.wireOp",EDGE,"E90.0.2"),sQuery(id+"F9.wireOp",EDGE,"E90.0.3"),sQuery(id+"F9.wireOp",EDGE,"E93"),sQuery(id+"F9.wireOp",EDGE,"E94"),sQuery(id+"F9.wireOp",EDGE,"E95"),sQuery(id+"F9.wireOp",EDGE,"E96"),sQuery(id+"F9.wireOp",EDGE,"E97"),sQuery(id+"F9.wireOp",EDGE,"E98"),sQuery(id+"F9.wireOp",EDGE,"E99"),sQuery(id+"F9.wireOp",EDGE,"E100"),sQuery(id+"F9.wireOp",EDGE,"E103"),sQuery(id+"F9.wireOp",EDGE,"E104"),sQuery(id+"F9.wireOp",EDGE,"E105"),sQuery(id+"F9.wireOp",EDGE,"E106"),sQuery(id+"F9.wireOp",EDGE,"E107"),sQuery(id+"F9.wireOp",EDGE,"E108"),sQuery(id+"F9.wireOp",EDGE,"E109"),sQuery(id+"F9.wireOp",EDGE,"E110"),sQuery(id+"F9.wireOp",EDGE,"E113.filletArc"),sQuery(id+"F9.wireOp",EDGE,"E114.filletArc"),sQuery(id+"F9.wireOp",EDGE,"E115.filletArc"),sQuery(id+"F9.wireOp",EDGE,"E116.filletArc"),sQuery(id+"F9.wireOp",EDGE,"E117.filletArc"),sQuery(id+"F9.wireOp",EDGE,"E118")])]});
            var Q1;
            Q1=qCreatedBy(makeId("Right.planeOp"),FACE);
            mirror(context, id + "F21", {"entities" : qUnion([Q0]), "mirrorPlane" : qUnion([Q1])});
        }
        {
            var Q0;
            Q0=makeQuery(id+"F14.boolean.opBoolean","COPY",FACE,{"derivedFrom":makeQuery(id+"F14.opExtrude","SWEPT_FACE",FACE,{"disambiguationData":[OSD([sQuery(id+"F13.wireOp",EDGE,"E127.right")])]})});
            var sketch = newSketch(context, id + "F22", { "sketchPlane" : qUnion([Q0])});
            skLineSegment(sketch, "E131.0", {"start": v(153.67, -38.1) * mm, "end": v(153.67, -63.5) * mm});
            skLineSegment(sketch, "E132.0", {"start": v(147.32, -63.5) * mm, "end": v(153.67, -63.5) * mm});
            skLineSegment(sketch, "E133.0", {"start": v(147.32, -38.1) * mm, "end": v(153.67, -38.1) * mm});
            skLineSegment(sketch, "E134", {"start": v(147.32, -38.1) * mm, "end": v(147.32, -25.15) * mm});
            skLineSegment(sketch, "E135", {"start": v(147.32, -25.15) * mm, "end": v(141.5, -22.44) * mm});
            skLineSegment(sketch, "E136", {"start": v(126.85, -53.87) * mm, "end": v(136, -58.14) * mm});
            skLineSegment(sketch, "E137", {"start": v(142.26, -64.52) * mm, "end": v(147.32, -75.97) * mm});
            skLineSegment(sketch, "E138", {"start": v(147.32, -75.97) * mm, "end": v(147.32, -63.5) * mm});
            skLineSegment(sketch, "E139", {"start": v(141.5, -22.44) * mm, "end": v(126.85, -53.87) * mm, "construction": true});
            skArc(sketch, "E140.trimOffspring", {"start": v(141.5, -22.44) * mm, "mid": v(118.46, -30.83) * mm, "end": v(126.85, -53.87) * mm});
            skPoint(sketch, "E141.visualSharp", {"position": v(140.33, -60.16) * mm});
            skArc(sketch, "E141.filletArc", {"start": v(142.26, -64.52) * mm, "mid": v(139.71, -60.76) * mm, "end": v(136, -58.14) * mm});
            skCircle(sketch, "E142", {"center": v(134.18, -38.15) * mm, "radius": 9.53 * mm, "construction": true});
            skCircle(sketch, "E143", {"center": v(138.2, -29.52) * mm, "radius": 1.75 * mm});
            skCircle(sketch, "E144.1.0", {"center": v(125.55, -34.13) * mm, "radius": 1.75 * mm});
            skCircle(sketch, "E144.2.0", {"center": v(130.16, -46.79) * mm, "radius": 1.75 * mm});
            skCircle(sketch, "E144.3.0", {"center": v(142.81, -42.18) * mm, "radius": 1.75 * mm});
            skSolve(sketch);
        }
        {
            var Q0;
            Q0=makeQuery(id+"F22.imprint","IMPRINT",FACE,{"disambiguationData":[TD([[makeQuery(id+"F22.imprint","IMPRINT",EDGE,{"derivedFrom":sQuery(id+"F22.wireOp",EDGE,"E134")}),1.0]])]});
            var Q1;
            Q1=makeQuery(id+"F22.imprint","IMPRINT",FACE,{"disambiguationData":[TD([[makeQuery(id+"F22.imprint","IMPRINT",EDGE,{"derivedFrom":sQuery(id+"F22.wireOp",EDGE,"E131.0")}),-1.0]])]});
            extrude(context, id + "F23", {"entities" : qUnion([Q0, Q1]), "depth" : 6.35 * mm, "offsetDistance" : 25.4 * mm});
        }
        {
            var Q0;
            Q0=makeQuery(id+"F23.opExtrude","SWEPT_BODY",BODY,{"disambiguationData":[OSD([sQuery(id+"F22.wireOp",EDGE,"E131.0"),sQuery(id+"F22.wireOp",EDGE,"E132.0"),sQuery(id+"F22.wireOp",EDGE,"E133.0"),sQuery(id+"F22.wireOp",EDGE,"E134"),sQuery(id+"F22.wireOp",EDGE,"E135"),sQuery(id+"F22.wireOp",EDGE,"E136"),sQuery(id+"F22.wireOp",EDGE,"E137"),sQuery(id+"F22.wireOp",EDGE,"E138"),sQuery(id+"F22.wireOp",EDGE,"E140.trimOffspring"),sQuery(id+"F22.wireOp",EDGE,"E141.filletArc"),sQuery(id+"F22.wireOp",EDGE,"E143"),sQuery(id+"F22.wireOp",EDGE,"E144.1.0"),sQuery(id+"F22.wireOp",EDGE,"E144.2.0"),sQuery(id+"F22.wireOp",EDGE,"E144.3.0")])]});
            var Q1;
            Q1=qCreatedBy(makeId("Right.planeOp"),FACE);
            mirror(context, id + "F24", {"operationType" : NewBodyOperationType.ADD, "entities" : qUnion([Q0]), "mirrorPlane" : qUnion([Q1])});
        }
    });
